# Revit family: Indirect-Water-Heater_AO_Smith-ITS-300_N_B
name_source: partatom
category: Mechanical Equipment
revit_build: Autodesk Revit 2014 (Build: 20130308_1515(x64)
units: mm (PartAtom-declared; Revit-internal decimal feet)

## types (1)
- Indirect-Water-Heater_AO_Smith-ITS-300_N_B
    1e Maintenance (check-up) = 3 maanden na installatie
    2nd Maintenance (general maintenance) = 12 maanden na installatie
    Assembly Code = D3010
    BIM Content Developer = CAD & Company
    BIM Content Developer URL = http://www.cadcompany.nl
    Cold Water Connection R = 1"
    Description = Indirecte Boiler met 2 warmtewisselaars
    Destination / Counrty = Nederland
    Diameter (with insulation) = 360 mm  [stored 1.1811 ft]
    Diameter (without insulation) = 303 mm  [stored 0.994094 ft]
    Draw-off Capacity @ ΔT = 28°C after 120 min. = 4950.0 L
    Draw-off Capacity @ ΔT = 28°C after 30 min. = 1587.0 L
    Draw-off Capacity @ ΔT = 28°C after 60 min. = 2708.0 L
    Draw-off Capacity @ ΔT = 28°C after 90 min. = 3829.0 L
    Draw-off Capacity @ ΔT = 44°C after 120 min. = 0.0 L
    Draw-off Capacity @ ΔT = 44°C after 30 min. = 0.0 L
    Draw-off Capacity @ ΔT = 44°C after 60 min. = 0.0 L
    Draw-off Capacity @ ΔT = 44°C after 90 min. = 0.0 L
    Draw-off Capacity @ ΔT = 50°C after 120 min. = 2772.0 L
    Draw-off Capacity @ ΔT = 50°C after 30 min. = 889.0 L
    Draw-off Capacity @ ΔT = 50°C after 60 min. = 1517.0 L
    Draw-off Capacity @ ΔT = 50°C after 90 min. = 2144.0 L
    Draw-off Capacity @ ΔT = 55°C after 120 min. = 0.0 L
    Draw-off Capacity @ ΔT = 55°C after 30 min. = 0.0 L
    Draw-off Capacity @ ΔT = 55°C after 60 min. = 0.0 L
    Draw-off Capacity @ ΔT = 55°C after 90 min. = 0.0 L
    Draw-off Capacity @ ΔT = 70°C after 120 min. = 1980.0 L
    Draw-off Capacity @ ΔT = 70°C after 30 min. = 635.0 L
    Draw-off Capacity @ ΔT = 70°C after 60 min. = 1083.0 L
    Draw-off Capacity @ ΔT = 70°C after 90 min. = 1532.0 L
    Empty Weight = 133.00 kg
    Flow Rate - bottom heat  exchanger 80ºC/60ºC = 1978
    Flow Rate - top heat  exchanger 80ºC/60ºC = 1161
    Heating Up Time @ ΔT = 28°C = 8
    Heating Up Time @ ΔT = 50°C = 14
    Heating Up Time @ ΔT = 70°C = 19
    Height (with insulation) = 1370 mm  [stored 4.49475 ft]
    Height (without insulation) = 1313 mm  [stored 4.30774 ft]
    Height Cold Water Inlet = 75 mm
    Height Warm Water Outlet = 1310 mm  [stored 4.2979 ft]
    Hot / Warm Water Connection R = 1"
    Insulation Thickness = 57 mm  [stored 0.187008 ft]
    Length = 0 mm  [stored 0 ft]
    Maintenance Interval = 12 maanden
    Manufacturer = A.O. Smith Water Products Company b.v.
    Manufacturer Number = E 7110
E 7110
E 7110
    Max. Operating Pressure - heat exchanger = 1600000.0 Pa
    Max. Operating Pressure - tank = 1000000.0 Pa
    Max. Temperature - heat exchanger = 110 °C
    Max. Temperature - tank = 95 °C
    Model = ITS 300 N B
    Nominal Output - bottom heat  exchanger = 46000 W
    Nominal Output - top heat  exchanger = 27000 W
    Operating Weight = 413.00 kg
    Packaging Height = 1510 mm  [stored 4.95407 ft]
    Packaging Length = 780 mm  [stored 2.55906 ft]
    Packaging Width = 780 mm  [stored 2.55906 ft]
    Pressure Loss - bottom heat  exchanger 80ºC/60ºC = 44000.0 Pa
    Pressure Loss - top heat  exchanger 80ºC/60ºC = 12000.0 Pa
    Product Documentation Link = https://www.aosmithinternational.com
    Product Instruction Link = https://www.aosmithinternational.com
    Recovery Rate @ ΔT = 28°C (ltr/hr) = 2242
    Recovery Rate @ ΔT = 44°C (ltr/hr) = 0
    Recovery Rate @ ΔT = 50°C (ltr/hr) = 1256
    Recovery Rate @ ΔT = 55°C (ltr/hr) = 0
    Recovery Rate @ ΔT = 70°C (ltr/hr) = 897
    Serial Number = 8717449181833
    Stand-by Loss = 0 W
    Stand-by Loss - daily (Watt/24H) = 0
    Storage Capacity - bottom heat  exchanger = 9.5 m³
    Storage Capacity - tank = 422 m³
    Storage Capacity - top heat  exchanger = 5.7 m³
    Surface Top Heat Exchanger = 0.85 m²
    Surface bottom heat  Exchanger = 1.45 m²
    T&P Connection Rp = 1"
    Transport Weight = 144.00 kg
    Type of Packaging = Plastic en Hout
    URL = www.aosmith.nl
    Warranty on Parts = 12 maanden
    Warranty on Tank = 36 maanden
    Width = 0 mm  [stored 0 ft]
    Workspace = 860 mm

note: [stored X ft] marks values corroborated as IEEE doubles in the binary element streams (Revit-internal decimal feet)

## geometry (parser evidence)
native form markers: Sweep x17
no freeform markers — native parametric forms only
